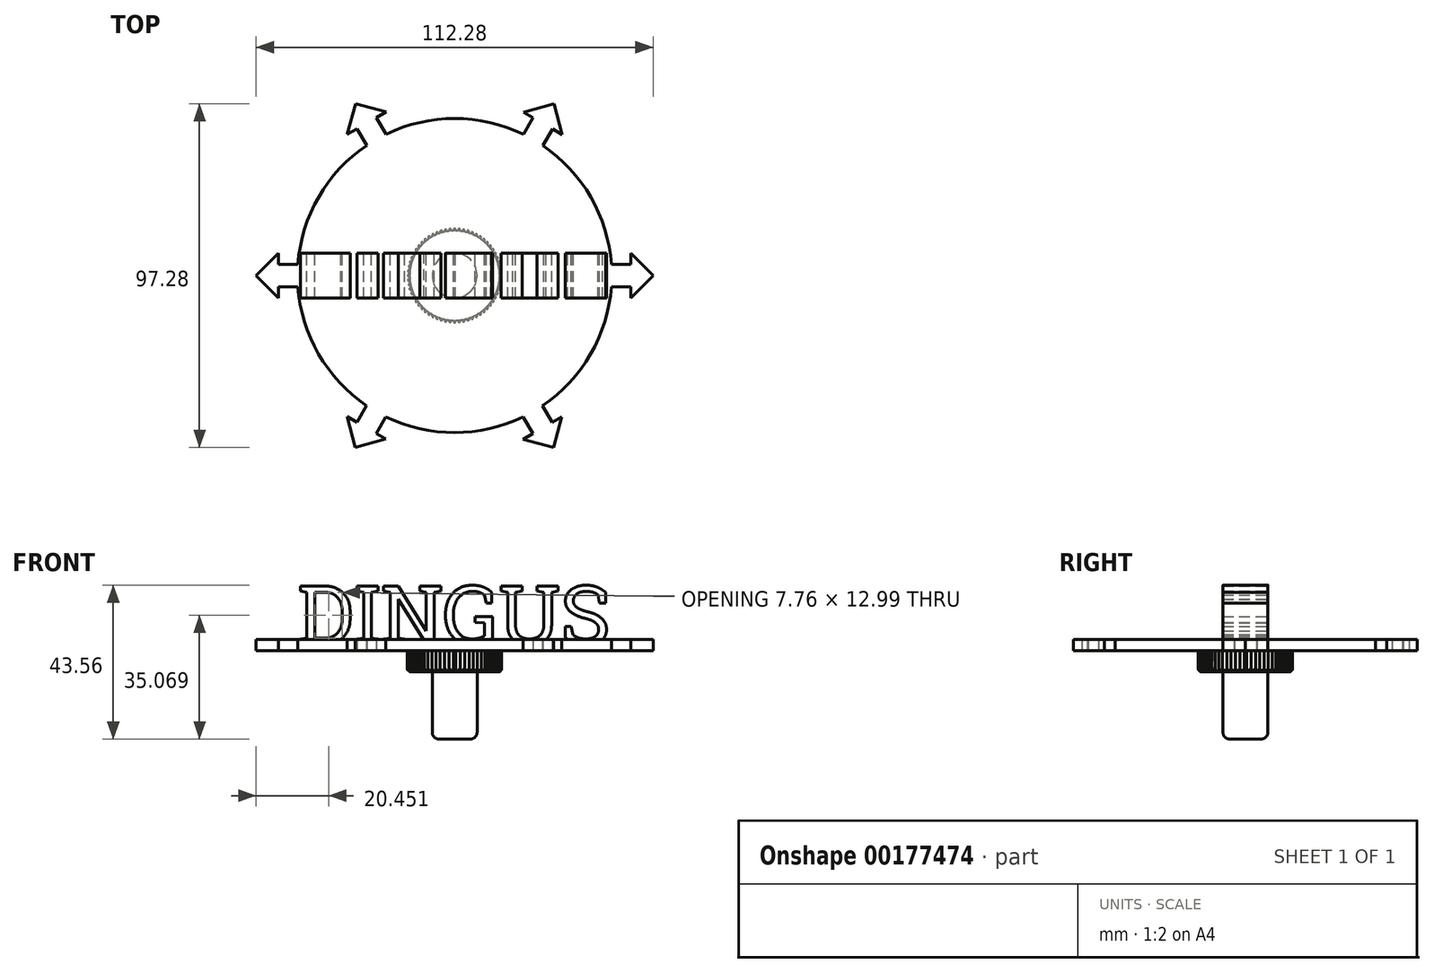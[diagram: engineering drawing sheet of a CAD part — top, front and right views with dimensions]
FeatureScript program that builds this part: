
annotation { "Feature Type Name" : "Feature", "Feature Type Description" : "" }
export const myFeature = defineFeature(function(context is Context, id is Id, definition is map)
    precondition{}
    {
        {
            var Q0;
            Q0=qCreatedBy(makeId("Top.planeOp"),FACE);
            var sketch = newSketch(context, id + "F0", { "sketchPlane" : qUnion([Q0])});
            skCircle(sketch, "E0", {"center": v(0, 0) * mm, "radius": 13.34 * mm, "construction": true});
            skCircle(sketch, "E1", {"center": v(0, 0) * mm, "radius": 12.7 * mm, "construction": true});
            skCircle(sketch, "E2", {"center": v(0, 0) * mm, "radius": 6.35 * mm, "construction": true});
            skLineSegment(sketch, "E3", {"start": v(0, 0) * mm, "end": v(0, 13.34) * mm});
            skLineSegment(sketch, "E4", {"start": v(0, 0) * mm, "end": v(-0.65, 13.32) * mm, "construction": true});
            skLineSegment(sketch, "E5", {"start": v(0, 0) * mm, "end": v(0.65, 13.32) * mm, "construction": true});
            skSolve(sketch);
        }
        {
            var Q0;
            Q0=qCreatedBy(makeId("Top.planeOp"),FACE);
            var sketch = newSketch(context, id + "F1", { "sketchPlane" : qUnion([Q0])});
            skArc(sketch, "E6", {"start": v(0.32, 13.01) * mm, "mid": v(0, 13.34) * mm, "end": v(-0.32, 13.01) * mm});
            skArc(sketch, "E7", {"start": v(-0.62, 12.68) * mm, "mid": v(-0.4, 12.79) * mm, "end": v(-0.32, 13.01) * mm});
            skArc(sketch, "E8", {"start": v(0.32, 13.01) * mm, "mid": v(0.4, 12.79) * mm, "end": v(0.62, 12.68) * mm});
            skArc(sketch, "E9", {"start": v(0.32, 13.01) * mm, "mid": v(0, 13.02) * mm, "end": v(-0.32, 13.01) * mm, "construction": true});
            skArc(sketch, "E10.1.0", {"start": v(-1.86, 12.56) * mm, "mid": v(-1.65, 12.69) * mm, "end": v(-1.59, 12.92) * mm});
            skArc(sketch, "E10.1.1", {"start": v(-0.96, 12.98) * mm, "mid": v(-1.3, 13.27) * mm, "end": v(-1.59, 12.92) * mm});
            skArc(sketch, "E10.1.2", {"start": v(-0.96, 12.98) * mm, "mid": v(-0.85, 12.76) * mm, "end": v(-0.62, 12.68) * mm});
            skArc(sketch, "E10.2.0", {"start": v(-3.09, 12.32) * mm, "mid": v(-2.89, 12.46) * mm, "end": v(-2.85, 12.7) * mm});
            skArc(sketch, "E10.2.1", {"start": v(-2.23, 12.83) * mm, "mid": v(-2.6, 13.08) * mm, "end": v(-2.85, 12.7) * mm});
            skArc(sketch, "E10.2.2", {"start": v(-2.23, 12.83) * mm, "mid": v(-2.1, 12.62) * mm, "end": v(-1.86, 12.56) * mm});
            skArc(sketch, "E10.3.0", {"start": v(-4.28, 11.96) * mm, "mid": v(-4.1, 12.12) * mm, "end": v(-4.08, 12.36) * mm});
            skArc(sketch, "E10.3.1", {"start": v(-3.48, 12.54) * mm, "mid": v(-3.87, 12.76) * mm, "end": v(-4.08, 12.36) * mm});
            skArc(sketch, "E10.3.2", {"start": v(-3.48, 12.54) * mm, "mid": v(-3.33, 12.35) * mm, "end": v(-3.09, 12.32) * mm});
            skArc(sketch, "E10.4.0", {"start": v(-5.43, 11.48) * mm, "mid": v(-5.27, 11.66) * mm, "end": v(-5.27, 11.9) * mm});
            skArc(sketch, "E10.4.1", {"start": v(-4.69, 12.14) * mm, "mid": v(-5.1, 12.32) * mm, "end": v(-5.27, 11.9) * mm});
            skArc(sketch, "E10.4.2", {"start": v(-4.69, 12.14) * mm, "mid": v(-4.52, 11.97) * mm, "end": v(-4.28, 11.96) * mm});
            skArc(sketch, "E10.5.0", {"start": v(-6.53, 10.9) * mm, "mid": v(-6.38, 11.09) * mm, "end": v(-6.41, 11.33) * mm});
            skArc(sketch, "E10.5.1", {"start": v(-5.86, 11.63) * mm, "mid": v(-6.29, 11.76) * mm, "end": v(-6.41, 11.33) * mm});
            skArc(sketch, "E10.5.2", {"start": v(-5.86, 11.63) * mm, "mid": v(-5.67, 11.47) * mm, "end": v(-5.43, 11.48) * mm});
            skArc(sketch, "E10.6.0", {"start": v(-7.57, 10.2) * mm, "mid": v(-7.44, 10.4) * mm, "end": v(-7.5, 10.65) * mm});
            skArc(sketch, "E10.6.1", {"start": v(-6.97, 11) * mm, "mid": v(-7.4, 11.09) * mm, "end": v(-7.5, 10.65) * mm});
            skArc(sketch, "E10.6.2", {"start": v(-6.97, 11) * mm, "mid": v(-6.77, 10.86) * mm, "end": v(-6.53, 10.9) * mm});
            skArc(sketch, "E10.7.0", {"start": v(-8.53, 9.41) * mm, "mid": v(-8.42, 9.63) * mm, "end": v(-8.5, 9.86) * mm});
            skArc(sketch, "E10.7.1", {"start": v(-8.01, 10.26) * mm, "mid": v(-8.46, 10.3) * mm, "end": v(-8.5, 9.86) * mm});
            skArc(sketch, "E10.7.2", {"start": v(-8.01, 10.26) * mm, "mid": v(-7.8, 10.14) * mm, "end": v(-7.57, 10.2) * mm});
            skArc(sketch, "E10.8.0", {"start": v(-9.41, 8.53) * mm, "mid": v(-9.33, 8.76) * mm, "end": v(-9.43, 8.98) * mm});
            skArc(sketch, "E10.8.1", {"start": v(-8.98, 9.43) * mm, "mid": v(-9.43, 9.43) * mm, "end": v(-9.43, 8.98) * mm});
            skArc(sketch, "E10.8.2", {"start": v(-8.98, 9.43) * mm, "mid": v(-8.76, 9.33) * mm, "end": v(-8.53, 9.41) * mm});
            skArc(sketch, "E10.9.0", {"start": v(-10.2, 7.57) * mm, "mid": v(-10.14, 7.8) * mm, "end": v(-10.26, 8.01) * mm});
            skArc(sketch, "E10.9.1", {"start": v(-9.86, 8.5) * mm, "mid": v(-10.3, 8.46) * mm, "end": v(-10.26, 8.01) * mm});
            skArc(sketch, "E10.9.2", {"start": v(-9.86, 8.5) * mm, "mid": v(-9.63, 8.42) * mm, "end": v(-9.41, 8.53) * mm});
            skArc(sketch, "E10.10.0", {"start": v(-10.9, 6.53) * mm, "mid": v(-10.86, 6.77) * mm, "end": v(-11, 6.97) * mm});
            skArc(sketch, "E10.10.1", {"start": v(-10.65, 7.5) * mm, "mid": v(-11.09, 7.4) * mm, "end": v(-11, 6.97) * mm});
            skArc(sketch, "E10.10.2", {"start": v(-10.65, 7.5) * mm, "mid": v(-10.4, 7.44) * mm, "end": v(-10.2, 7.57) * mm});
            skArc(sketch, "E10.11.0", {"start": v(-11.48, 5.43) * mm, "mid": v(-11.47, 5.67) * mm, "end": v(-11.63, 5.86) * mm});
            skArc(sketch, "E10.11.1", {"start": v(-11.33, 6.41) * mm, "mid": v(-11.76, 6.29) * mm, "end": v(-11.63, 5.86) * mm});
            skArc(sketch, "E10.11.2", {"start": v(-11.33, 6.41) * mm, "mid": v(-11.09, 6.38) * mm, "end": v(-10.9, 6.53) * mm});
            skArc(sketch, "E10.12.0", {"start": v(-11.96, 4.28) * mm, "mid": v(-11.97, 4.52) * mm, "end": v(-12.14, 4.69) * mm});
            skArc(sketch, "E10.12.1", {"start": v(-11.9, 5.27) * mm, "mid": v(-12.32, 5.1) * mm, "end": v(-12.14, 4.69) * mm});
            skArc(sketch, "E10.12.2", {"start": v(-11.9, 5.27) * mm, "mid": v(-11.66, 5.27) * mm, "end": v(-11.48, 5.43) * mm});
            skArc(sketch, "E10.13.0", {"start": v(-12.32, 3.09) * mm, "mid": v(-12.35, 3.33) * mm, "end": v(-12.54, 3.48) * mm});
            skArc(sketch, "E10.13.1", {"start": v(-12.36, 4.08) * mm, "mid": v(-12.76, 3.87) * mm, "end": v(-12.54, 3.48) * mm});
            skArc(sketch, "E10.13.2", {"start": v(-12.36, 4.08) * mm, "mid": v(-12.12, 4.1) * mm, "end": v(-11.96, 4.28) * mm});
            skArc(sketch, "E10.14.0", {"start": v(-12.56, 1.86) * mm, "mid": v(-12.62, 2.1) * mm, "end": v(-12.83, 2.23) * mm});
            skArc(sketch, "E10.14.1", {"start": v(-12.7, 2.85) * mm, "mid": v(-13.08, 2.6) * mm, "end": v(-12.83, 2.23) * mm});
            skArc(sketch, "E10.14.2", {"start": v(-12.7, 2.85) * mm, "mid": v(-12.46, 2.89) * mm, "end": v(-12.32, 3.09) * mm});
            skArc(sketch, "E10.15.0", {"start": v(-12.68, 0.62) * mm, "mid": v(-12.76, 0.85) * mm, "end": v(-12.98, 0.96) * mm});
            skArc(sketch, "E10.15.1", {"start": v(-12.92, 1.59) * mm, "mid": v(-13.27, 1.3) * mm, "end": v(-12.98, 0.96) * mm});
            skArc(sketch, "E10.15.2", {"start": v(-12.92, 1.59) * mm, "mid": v(-12.69, 1.65) * mm, "end": v(-12.56, 1.86) * mm});
            skArc(sketch, "E10.16.0", {"start": v(-12.68, -0.62) * mm, "mid": v(-12.79, -0.4) * mm, "end": v(-13.01, -0.32) * mm});
            skArc(sketch, "E10.16.1", {"start": v(-13.01, 0.32) * mm, "mid": v(-13.34, 0) * mm, "end": v(-13.01, -0.32) * mm});
            skArc(sketch, "E10.16.2", {"start": v(-13.01, 0.32) * mm, "mid": v(-12.79, 0.4) * mm, "end": v(-12.68, 0.62) * mm});
            skArc(sketch, "E10.17.0", {"start": v(-12.56, -1.86) * mm, "mid": v(-12.69, -1.65) * mm, "end": v(-12.92, -1.59) * mm});
            skArc(sketch, "E10.17.1", {"start": v(-12.98, -0.96) * mm, "mid": v(-13.27, -1.3) * mm, "end": v(-12.92, -1.59) * mm});
            skArc(sketch, "E10.17.2", {"start": v(-12.98, -0.96) * mm, "mid": v(-12.76, -0.85) * mm, "end": v(-12.68, -0.62) * mm});
            skArc(sketch, "E10.18.0", {"start": v(-12.32, -3.09) * mm, "mid": v(-12.46, -2.89) * mm, "end": v(-12.7, -2.85) * mm});
            skArc(sketch, "E10.18.1", {"start": v(-12.83, -2.23) * mm, "mid": v(-13.08, -2.6) * mm, "end": v(-12.7, -2.85) * mm});
            skArc(sketch, "E10.18.2", {"start": v(-12.83, -2.23) * mm, "mid": v(-12.62, -2.1) * mm, "end": v(-12.56, -1.86) * mm});
            skArc(sketch, "E10.19.0", {"start": v(-11.96, -4.28) * mm, "mid": v(-12.12, -4.1) * mm, "end": v(-12.36, -4.08) * mm});
            skArc(sketch, "E10.19.1", {"start": v(-12.54, -3.48) * mm, "mid": v(-12.76, -3.87) * mm, "end": v(-12.36, -4.08) * mm});
            skArc(sketch, "E10.19.2", {"start": v(-12.54, -3.48) * mm, "mid": v(-12.35, -3.33) * mm, "end": v(-12.32, -3.09) * mm});
            skArc(sketch, "E10.20.0", {"start": v(-11.48, -5.43) * mm, "mid": v(-11.66, -5.27) * mm, "end": v(-11.9, -5.27) * mm});
            skArc(sketch, "E10.20.1", {"start": v(-12.14, -4.69) * mm, "mid": v(-12.32, -5.1) * mm, "end": v(-11.9, -5.27) * mm});
            skArc(sketch, "E10.20.2", {"start": v(-12.14, -4.69) * mm, "mid": v(-11.97, -4.52) * mm, "end": v(-11.96, -4.28) * mm});
            skArc(sketch, "E10.21.0", {"start": v(-10.9, -6.53) * mm, "mid": v(-11.09, -6.38) * mm, "end": v(-11.33, -6.41) * mm});
            skArc(sketch, "E10.21.1", {"start": v(-11.63, -5.86) * mm, "mid": v(-11.76, -6.29) * mm, "end": v(-11.33, -6.41) * mm});
            skArc(sketch, "E10.21.2", {"start": v(-11.63, -5.86) * mm, "mid": v(-11.47, -5.67) * mm, "end": v(-11.48, -5.43) * mm});
            skArc(sketch, "E10.22.0", {"start": v(-10.2, -7.57) * mm, "mid": v(-10.4, -7.44) * mm, "end": v(-10.65, -7.5) * mm});
            skArc(sketch, "E10.22.1", {"start": v(-11, -6.97) * mm, "mid": v(-11.09, -7.4) * mm, "end": v(-10.65, -7.5) * mm});
            skArc(sketch, "E10.22.2", {"start": v(-11, -6.97) * mm, "mid": v(-10.86, -6.77) * mm, "end": v(-10.9, -6.53) * mm});
            skArc(sketch, "E10.23.0", {"start": v(-9.41, -8.53) * mm, "mid": v(-9.63, -8.42) * mm, "end": v(-9.86, -8.5) * mm});
            skArc(sketch, "E10.23.1", {"start": v(-10.26, -8.01) * mm, "mid": v(-10.3, -8.46) * mm, "end": v(-9.86, -8.5) * mm});
            skArc(sketch, "E10.23.2", {"start": v(-10.26, -8.01) * mm, "mid": v(-10.14, -7.8) * mm, "end": v(-10.2, -7.57) * mm});
            skArc(sketch, "E10.24.0", {"start": v(-8.53, -9.41) * mm, "mid": v(-8.76, -9.33) * mm, "end": v(-8.98, -9.43) * mm});
            skArc(sketch, "E10.24.1", {"start": v(-9.43, -8.98) * mm, "mid": v(-9.43, -9.43) * mm, "end": v(-8.98, -9.43) * mm});
            skArc(sketch, "E10.24.2", {"start": v(-9.43, -8.98) * mm, "mid": v(-9.33, -8.76) * mm, "end": v(-9.41, -8.53) * mm});
            skArc(sketch, "E10.25.0", {"start": v(-7.57, -10.2) * mm, "mid": v(-7.8, -10.14) * mm, "end": v(-8.01, -10.26) * mm});
            skArc(sketch, "E10.25.1", {"start": v(-8.5, -9.86) * mm, "mid": v(-8.46, -10.3) * mm, "end": v(-8.01, -10.26) * mm});
            skArc(sketch, "E10.25.2", {"start": v(-8.5, -9.86) * mm, "mid": v(-8.42, -9.63) * mm, "end": v(-8.53, -9.41) * mm});
            skArc(sketch, "E10.26.0", {"start": v(-6.53, -10.9) * mm, "mid": v(-6.77, -10.86) * mm, "end": v(-6.97, -11) * mm});
            skArc(sketch, "E10.26.1", {"start": v(-7.5, -10.65) * mm, "mid": v(-7.4, -11.09) * mm, "end": v(-6.97, -11) * mm});
            skArc(sketch, "E10.26.2", {"start": v(-7.5, -10.65) * mm, "mid": v(-7.44, -10.4) * mm, "end": v(-7.57, -10.2) * mm});
            skArc(sketch, "E10.27.0", {"start": v(-5.43, -11.48) * mm, "mid": v(-5.67, -11.47) * mm, "end": v(-5.86, -11.63) * mm});
            skArc(sketch, "E10.27.1", {"start": v(-6.41, -11.33) * mm, "mid": v(-6.29, -11.76) * mm, "end": v(-5.86, -11.63) * mm});
            skArc(sketch, "E10.27.2", {"start": v(-6.41, -11.33) * mm, "mid": v(-6.38, -11.09) * mm, "end": v(-6.53, -10.9) * mm});
            skArc(sketch, "E10.28.0", {"start": v(-4.28, -11.96) * mm, "mid": v(-4.52, -11.97) * mm, "end": v(-4.69, -12.14) * mm});
            skArc(sketch, "E10.28.1", {"start": v(-5.27, -11.9) * mm, "mid": v(-5.1, -12.32) * mm, "end": v(-4.69, -12.14) * mm});
            skArc(sketch, "E10.28.2", {"start": v(-5.27, -11.9) * mm, "mid": v(-5.27, -11.66) * mm, "end": v(-5.43, -11.48) * mm});
            skArc(sketch, "E10.29.0", {"start": v(-3.09, -12.32) * mm, "mid": v(-3.33, -12.35) * mm, "end": v(-3.48, -12.54) * mm});
            skArc(sketch, "E10.29.1", {"start": v(-4.08, -12.36) * mm, "mid": v(-3.87, -12.76) * mm, "end": v(-3.48, -12.54) * mm});
            skArc(sketch, "E10.29.2", {"start": v(-4.08, -12.36) * mm, "mid": v(-4.1, -12.12) * mm, "end": v(-4.28, -11.96) * mm});
            skArc(sketch, "E10.30.0", {"start": v(-1.86, -12.56) * mm, "mid": v(-2.1, -12.62) * mm, "end": v(-2.23, -12.83) * mm});
            skArc(sketch, "E10.30.1", {"start": v(-2.85, -12.7) * mm, "mid": v(-2.6, -13.08) * mm, "end": v(-2.23, -12.83) * mm});
            skArc(sketch, "E10.30.2", {"start": v(-2.85, -12.7) * mm, "mid": v(-2.89, -12.46) * mm, "end": v(-3.09, -12.32) * mm});
            skArc(sketch, "E10.31.0", {"start": v(-0.62, -12.68) * mm, "mid": v(-0.85, -12.76) * mm, "end": v(-0.96, -12.98) * mm});
            skArc(sketch, "E10.31.1", {"start": v(-1.59, -12.92) * mm, "mid": v(-1.3, -13.27) * mm, "end": v(-0.96, -12.98) * mm});
            skArc(sketch, "E10.31.2", {"start": v(-1.59, -12.92) * mm, "mid": v(-1.65, -12.69) * mm, "end": v(-1.86, -12.56) * mm});
            skPoint(sketch, "E10.center", {"position": v(0, 0) * mm});
            skArc(sketch, "E11.2.32.0", {"start": v(0.62, -12.68) * mm, "mid": v(0.4, -12.79) * mm, "end": v(0.32, -13.01) * mm});
            skArc(sketch, "E11.4.32.0", {"start": v(-0.32, -13.01) * mm, "mid": v(0, -13.34) * mm, "end": v(0.32, -13.01) * mm});
            skArc(sketch, "E11.8.32.0", {"start": v(-0.32, -13.01) * mm, "mid": v(-0.4, -12.79) * mm, "end": v(-0.62, -12.68) * mm});
            skArc(sketch, "E11.2.33.0", {"start": v(1.86, -12.56) * mm, "mid": v(1.65, -12.69) * mm, "end": v(1.59, -12.92) * mm});
            skArc(sketch, "E11.4.33.0", {"start": v(0.96, -12.98) * mm, "mid": v(1.3, -13.27) * mm, "end": v(1.59, -12.92) * mm});
            skArc(sketch, "E11.8.33.0", {"start": v(0.96, -12.98) * mm, "mid": v(0.85, -12.76) * mm, "end": v(0.62, -12.68) * mm});
            skArc(sketch, "E11.2.34.0", {"start": v(3.09, -12.32) * mm, "mid": v(2.89, -12.46) * mm, "end": v(2.85, -12.7) * mm});
            skArc(sketch, "E11.4.34.0", {"start": v(2.23, -12.83) * mm, "mid": v(2.6, -13.08) * mm, "end": v(2.85, -12.7) * mm});
            skArc(sketch, "E11.8.34.0", {"start": v(2.23, -12.83) * mm, "mid": v(2.1, -12.62) * mm, "end": v(1.86, -12.56) * mm});
            skArc(sketch, "E11.2.35.0", {"start": v(4.28, -11.96) * mm, "mid": v(4.1, -12.12) * mm, "end": v(4.08, -12.36) * mm});
            skArc(sketch, "E11.4.35.0", {"start": v(3.48, -12.54) * mm, "mid": v(3.87, -12.76) * mm, "end": v(4.08, -12.36) * mm});
            skArc(sketch, "E11.8.35.0", {"start": v(3.48, -12.54) * mm, "mid": v(3.33, -12.35) * mm, "end": v(3.09, -12.32) * mm});
            skArc(sketch, "E11.2.36.0", {"start": v(5.43, -11.48) * mm, "mid": v(5.27, -11.66) * mm, "end": v(5.27, -11.9) * mm});
            skArc(sketch, "E11.4.36.0", {"start": v(4.69, -12.14) * mm, "mid": v(5.1, -12.32) * mm, "end": v(5.27, -11.9) * mm});
            skArc(sketch, "E11.8.36.0", {"start": v(4.69, -12.14) * mm, "mid": v(4.52, -11.97) * mm, "end": v(4.28, -11.96) * mm});
            skArc(sketch, "E11.2.37.0", {"start": v(6.53, -10.9) * mm, "mid": v(6.38, -11.09) * mm, "end": v(6.41, -11.33) * mm});
            skArc(sketch, "E11.4.37.0", {"start": v(5.86, -11.63) * mm, "mid": v(6.29, -11.76) * mm, "end": v(6.41, -11.33) * mm});
            skArc(sketch, "E11.8.37.0", {"start": v(5.86, -11.63) * mm, "mid": v(5.67, -11.47) * mm, "end": v(5.43, -11.48) * mm});
            skArc(sketch, "E11.2.38.0", {"start": v(7.57, -10.2) * mm, "mid": v(7.44, -10.4) * mm, "end": v(7.5, -10.65) * mm});
            skArc(sketch, "E11.4.38.0", {"start": v(6.97, -11) * mm, "mid": v(7.4, -11.09) * mm, "end": v(7.5, -10.65) * mm});
            skArc(sketch, "E11.8.38.0", {"start": v(6.97, -11) * mm, "mid": v(6.77, -10.86) * mm, "end": v(6.53, -10.9) * mm});
            skArc(sketch, "E11.2.39.0", {"start": v(8.53, -9.41) * mm, "mid": v(8.42, -9.63) * mm, "end": v(8.5, -9.86) * mm});
            skArc(sketch, "E11.4.39.0", {"start": v(8.01, -10.26) * mm, "mid": v(8.46, -10.3) * mm, "end": v(8.5, -9.86) * mm});
            skArc(sketch, "E11.8.39.0", {"start": v(8.01, -10.26) * mm, "mid": v(7.8, -10.14) * mm, "end": v(7.57, -10.2) * mm});
            skArc(sketch, "E11.2.40.0", {"start": v(9.41, -8.53) * mm, "mid": v(9.33, -8.76) * mm, "end": v(9.43, -8.98) * mm});
            skArc(sketch, "E11.4.40.0", {"start": v(8.98, -9.43) * mm, "mid": v(9.43, -9.43) * mm, "end": v(9.43, -8.98) * mm});
            skArc(sketch, "E11.8.40.0", {"start": v(8.98, -9.43) * mm, "mid": v(8.76, -9.33) * mm, "end": v(8.53, -9.41) * mm});
            skArc(sketch, "E11.2.41.0", {"start": v(10.2, -7.57) * mm, "mid": v(10.14, -7.8) * mm, "end": v(10.26, -8.01) * mm});
            skArc(sketch, "E11.4.41.0", {"start": v(9.86, -8.5) * mm, "mid": v(10.3, -8.46) * mm, "end": v(10.26, -8.01) * mm});
            skArc(sketch, "E11.8.41.0", {"start": v(9.86, -8.5) * mm, "mid": v(9.63, -8.42) * mm, "end": v(9.41, -8.53) * mm});
            skArc(sketch, "E11.2.42.0", {"start": v(10.9, -6.53) * mm, "mid": v(10.86, -6.77) * mm, "end": v(11, -6.97) * mm});
            skArc(sketch, "E11.4.42.0", {"start": v(10.65, -7.5) * mm, "mid": v(11.09, -7.4) * mm, "end": v(11, -6.97) * mm});
            skArc(sketch, "E11.8.42.0", {"start": v(10.65, -7.5) * mm, "mid": v(10.4, -7.44) * mm, "end": v(10.2, -7.57) * mm});
            skArc(sketch, "E11.2.43.0", {"start": v(11.48, -5.43) * mm, "mid": v(11.47, -5.67) * mm, "end": v(11.63, -5.86) * mm});
            skArc(sketch, "E11.4.43.0", {"start": v(11.33, -6.41) * mm, "mid": v(11.76, -6.29) * mm, "end": v(11.63, -5.86) * mm});
            skArc(sketch, "E11.8.43.0", {"start": v(11.33, -6.41) * mm, "mid": v(11.09, -6.38) * mm, "end": v(10.9, -6.53) * mm});
            skArc(sketch, "E11.2.44.0", {"start": v(11.96, -4.28) * mm, "mid": v(11.97, -4.52) * mm, "end": v(12.14, -4.69) * mm});
            skArc(sketch, "E11.4.44.0", {"start": v(11.9, -5.27) * mm, "mid": v(12.32, -5.1) * mm, "end": v(12.14, -4.69) * mm});
            skArc(sketch, "E11.8.44.0", {"start": v(11.9, -5.27) * mm, "mid": v(11.66, -5.27) * mm, "end": v(11.48, -5.43) * mm});
            skArc(sketch, "E11.2.45.0", {"start": v(12.32, -3.09) * mm, "mid": v(12.35, -3.33) * mm, "end": v(12.54, -3.48) * mm});
            skArc(sketch, "E11.4.45.0", {"start": v(12.36, -4.08) * mm, "mid": v(12.76, -3.87) * mm, "end": v(12.54, -3.48) * mm});
            skArc(sketch, "E11.8.45.0", {"start": v(12.36, -4.08) * mm, "mid": v(12.12, -4.1) * mm, "end": v(11.96, -4.28) * mm});
            skArc(sketch, "E11.2.46.0", {"start": v(12.56, -1.86) * mm, "mid": v(12.62, -2.1) * mm, "end": v(12.83, -2.23) * mm});
            skArc(sketch, "E11.4.46.0", {"start": v(12.7, -2.85) * mm, "mid": v(13.08, -2.6) * mm, "end": v(12.83, -2.23) * mm});
            skArc(sketch, "E11.8.46.0", {"start": v(12.7, -2.85) * mm, "mid": v(12.46, -2.89) * mm, "end": v(12.32, -3.09) * mm});
            skArc(sketch, "E11.2.47.0", {"start": v(12.68, -0.62) * mm, "mid": v(12.76, -0.85) * mm, "end": v(12.98, -0.96) * mm});
            skArc(sketch, "E11.4.47.0", {"start": v(12.92, -1.59) * mm, "mid": v(13.27, -1.3) * mm, "end": v(12.98, -0.96) * mm});
            skArc(sketch, "E11.8.47.0", {"start": v(12.92, -1.59) * mm, "mid": v(12.69, -1.65) * mm, "end": v(12.56, -1.86) * mm});
            skArc(sketch, "E11.2.48.0", {"start": v(12.68, 0.62) * mm, "mid": v(12.79, 0.4) * mm, "end": v(13.01, 0.32) * mm});
            skArc(sketch, "E11.4.48.0", {"start": v(13.01, -0.32) * mm, "mid": v(13.34, 0) * mm, "end": v(13.01, 0.32) * mm});
            skArc(sketch, "E11.8.48.0", {"start": v(13.01, -0.32) * mm, "mid": v(12.79, -0.4) * mm, "end": v(12.68, -0.62) * mm});
            skArc(sketch, "E11.2.49.0", {"start": v(12.56, 1.86) * mm, "mid": v(12.69, 1.65) * mm, "end": v(12.92, 1.59) * mm});
            skArc(sketch, "E11.4.49.0", {"start": v(12.98, 0.96) * mm, "mid": v(13.27, 1.3) * mm, "end": v(12.92, 1.59) * mm});
            skArc(sketch, "E11.8.49.0", {"start": v(12.98, 0.96) * mm, "mid": v(12.76, 0.85) * mm, "end": v(12.68, 0.62) * mm});
            skArc(sketch, "E11.2.50.0", {"start": v(12.32, 3.09) * mm, "mid": v(12.46, 2.89) * mm, "end": v(12.7, 2.85) * mm});
            skArc(sketch, "E11.4.50.0", {"start": v(12.83, 2.23) * mm, "mid": v(13.08, 2.6) * mm, "end": v(12.7, 2.85) * mm});
            skArc(sketch, "E11.8.50.0", {"start": v(12.83, 2.23) * mm, "mid": v(12.62, 2.1) * mm, "end": v(12.56, 1.86) * mm});
            skArc(sketch, "E11.2.51.0", {"start": v(11.96, 4.28) * mm, "mid": v(12.12, 4.1) * mm, "end": v(12.36, 4.08) * mm});
            skArc(sketch, "E11.4.51.0", {"start": v(12.54, 3.48) * mm, "mid": v(12.76, 3.87) * mm, "end": v(12.36, 4.08) * mm});
            skArc(sketch, "E11.8.51.0", {"start": v(12.54, 3.48) * mm, "mid": v(12.35, 3.33) * mm, "end": v(12.32, 3.09) * mm});
            skArc(sketch, "E11.2.52.0", {"start": v(11.48, 5.43) * mm, "mid": v(11.66, 5.27) * mm, "end": v(11.9, 5.27) * mm});
            skArc(sketch, "E11.4.52.0", {"start": v(12.14, 4.69) * mm, "mid": v(12.32, 5.1) * mm, "end": v(11.9, 5.27) * mm});
            skArc(sketch, "E11.8.52.0", {"start": v(12.14, 4.69) * mm, "mid": v(11.97, 4.52) * mm, "end": v(11.96, 4.28) * mm});
            skArc(sketch, "E11.2.53.0", {"start": v(10.9, 6.53) * mm, "mid": v(11.09, 6.38) * mm, "end": v(11.33, 6.41) * mm});
            skArc(sketch, "E11.4.53.0", {"start": v(11.63, 5.86) * mm, "mid": v(11.76, 6.29) * mm, "end": v(11.33, 6.41) * mm});
            skArc(sketch, "E11.8.53.0", {"start": v(11.63, 5.86) * mm, "mid": v(11.47, 5.67) * mm, "end": v(11.48, 5.43) * mm});
            skArc(sketch, "E11.2.54.0", {"start": v(10.2, 7.57) * mm, "mid": v(10.4, 7.44) * mm, "end": v(10.65, 7.5) * mm});
            skArc(sketch, "E11.4.54.0", {"start": v(11, 6.97) * mm, "mid": v(11.09, 7.4) * mm, "end": v(10.65, 7.5) * mm});
            skArc(sketch, "E11.8.54.0", {"start": v(11, 6.97) * mm, "mid": v(10.86, 6.77) * mm, "end": v(10.9, 6.53) * mm});
            skArc(sketch, "E11.2.55.0", {"start": v(9.41, 8.53) * mm, "mid": v(9.63, 8.42) * mm, "end": v(9.86, 8.5) * mm});
            skArc(sketch, "E11.4.55.0", {"start": v(10.26, 8.01) * mm, "mid": v(10.3, 8.46) * mm, "end": v(9.86, 8.5) * mm});
            skArc(sketch, "E11.8.55.0", {"start": v(10.26, 8.01) * mm, "mid": v(10.14, 7.8) * mm, "end": v(10.2, 7.57) * mm});
            skArc(sketch, "E11.2.56.0", {"start": v(8.53, 9.41) * mm, "mid": v(8.76, 9.33) * mm, "end": v(8.98, 9.43) * mm});
            skArc(sketch, "E11.4.56.0", {"start": v(9.43, 8.98) * mm, "mid": v(9.43, 9.43) * mm, "end": v(8.98, 9.43) * mm});
            skArc(sketch, "E11.8.56.0", {"start": v(9.43, 8.98) * mm, "mid": v(9.33, 8.76) * mm, "end": v(9.41, 8.53) * mm});
            skArc(sketch, "E11.2.57.0", {"start": v(7.57, 10.2) * mm, "mid": v(7.8, 10.14) * mm, "end": v(8.01, 10.26) * mm});
            skArc(sketch, "E11.4.57.0", {"start": v(8.5, 9.86) * mm, "mid": v(8.46, 10.3) * mm, "end": v(8.01, 10.26) * mm});
            skArc(sketch, "E11.8.57.0", {"start": v(8.5, 9.86) * mm, "mid": v(8.42, 9.63) * mm, "end": v(8.53, 9.41) * mm});
            skArc(sketch, "E11.2.58.0", {"start": v(6.53, 10.9) * mm, "mid": v(6.77, 10.86) * mm, "end": v(6.97, 11) * mm});
            skArc(sketch, "E11.4.58.0", {"start": v(7.5, 10.65) * mm, "mid": v(7.4, 11.09) * mm, "end": v(6.97, 11) * mm});
            skArc(sketch, "E11.8.58.0", {"start": v(7.5, 10.65) * mm, "mid": v(7.44, 10.4) * mm, "end": v(7.57, 10.2) * mm});
            skArc(sketch, "E11.2.59.0", {"start": v(5.43, 11.48) * mm, "mid": v(5.67, 11.47) * mm, "end": v(5.86, 11.63) * mm});
            skArc(sketch, "E11.4.59.0", {"start": v(6.41, 11.33) * mm, "mid": v(6.29, 11.76) * mm, "end": v(5.86, 11.63) * mm});
            skArc(sketch, "E11.8.59.0", {"start": v(6.41, 11.33) * mm, "mid": v(6.38, 11.09) * mm, "end": v(6.53, 10.9) * mm});
            skArc(sketch, "E11.2.60.0", {"start": v(4.28, 11.96) * mm, "mid": v(4.52, 11.97) * mm, "end": v(4.69, 12.14) * mm});
            skArc(sketch, "E11.4.60.0", {"start": v(5.27, 11.9) * mm, "mid": v(5.1, 12.32) * mm, "end": v(4.69, 12.14) * mm});
            skArc(sketch, "E11.8.60.0", {"start": v(5.27, 11.9) * mm, "mid": v(5.27, 11.66) * mm, "end": v(5.43, 11.48) * mm});
            skArc(sketch, "E11.2.61.0", {"start": v(3.09, 12.32) * mm, "mid": v(3.33, 12.35) * mm, "end": v(3.48, 12.54) * mm});
            skArc(sketch, "E11.4.61.0", {"start": v(4.08, 12.36) * mm, "mid": v(3.87, 12.76) * mm, "end": v(3.48, 12.54) * mm});
            skArc(sketch, "E11.8.61.0", {"start": v(4.08, 12.36) * mm, "mid": v(4.1, 12.12) * mm, "end": v(4.28, 11.96) * mm});
            skArc(sketch, "E11.2.62.0", {"start": v(1.86, 12.56) * mm, "mid": v(2.1, 12.62) * mm, "end": v(2.23, 12.83) * mm});
            skArc(sketch, "E11.4.62.0", {"start": v(2.85, 12.7) * mm, "mid": v(2.6, 13.08) * mm, "end": v(2.23, 12.83) * mm});
            skArc(sketch, "E11.8.62.0", {"start": v(2.85, 12.7) * mm, "mid": v(2.89, 12.46) * mm, "end": v(3.09, 12.32) * mm});
            skArc(sketch, "E11.2.63.0", {"start": v(0.62, 12.68) * mm, "mid": v(0.85, 12.76) * mm, "end": v(0.96, 12.98) * mm});
            skArc(sketch, "E11.4.63.0", {"start": v(1.59, 12.92) * mm, "mid": v(1.3, 13.27) * mm, "end": v(0.96, 12.98) * mm});
            skArc(sketch, "E11.8.63.0", {"start": v(1.59, 12.92) * mm, "mid": v(1.65, 12.69) * mm, "end": v(1.86, 12.56) * mm});
            skSolve(sketch);
        }
        {
            var Q0;
            Q0=makeQuery(id+"F1.imprint","IMPRINT",FACE,{"disambiguationData":[TD([[makeQuery(id+"F1.imprint","IMPRINT",EDGE,{"derivedFrom":sQuery(id+"F1.wireOp",EDGE,"E6")}),1.0]])]});
            extrude(context, id + "F2", {"entities" : qUnion([Q0]), "depth" : 6 * mm});
        }
        {
            var Q0;
            Q0=makeQuery(id+"F2.opExtrude","CAP_FACE",FACE,{"disambiguationData":[OSD([sQuery(id+"F1.wireOp",EDGE,"E6"),sQuery(id+"F1.wireOp",EDGE,"E7"),sQuery(id+"F1.wireOp",EDGE,"E8"),sQuery(id+"F1.wireOp",EDGE,"E10.1.0"),sQuery(id+"F1.wireOp",EDGE,"E10.1.1"),sQuery(id+"F1.wireOp",EDGE,"E10.1.2"),sQuery(id+"F1.wireOp",EDGE,"E10.2.0"),sQuery(id+"F1.wireOp",EDGE,"E10.2.1"),sQuery(id+"F1.wireOp",EDGE,"E10.2.2"),sQuery(id+"F1.wireOp",EDGE,"E10.3.0"),sQuery(id+"F1.wireOp",EDGE,"E10.3.1"),sQuery(id+"F1.wireOp",EDGE,"E10.3.2"),sQuery(id+"F1.wireOp",EDGE,"E10.4.0"),sQuery(id+"F1.wireOp",EDGE,"E10.4.1"),sQuery(id+"F1.wireOp",EDGE,"E10.4.2"),sQuery(id+"F1.wireOp",EDGE,"E10.5.0"),sQuery(id+"F1.wireOp",EDGE,"E10.5.1"),sQuery(id+"F1.wireOp",EDGE,"E10.5.2"),sQuery(id+"F1.wireOp",EDGE,"E10.6.0"),sQuery(id+"F1.wireOp",EDGE,"E10.6.1"),sQuery(id+"F1.wireOp",EDGE,"E10.6.2"),sQuery(id+"F1.wireOp",EDGE,"E10.7.0"),sQuery(id+"F1.wireOp",EDGE,"E10.7.1"),sQuery(id+"F1.wireOp",EDGE,"E10.7.2"),sQuery(id+"F1.wireOp",EDGE,"E10.8.0"),sQuery(id+"F1.wireOp",EDGE,"E10.8.1"),sQuery(id+"F1.wireOp",EDGE,"E10.8.2"),sQuery(id+"F1.wireOp",EDGE,"E10.9.0"),sQuery(id+"F1.wireOp",EDGE,"E10.9.1"),sQuery(id+"F1.wireOp",EDGE,"E10.9.2"),sQuery(id+"F1.wireOp",EDGE,"E10.10.0"),sQuery(id+"F1.wireOp",EDGE,"E10.10.1"),sQuery(id+"F1.wireOp",EDGE,"E10.10.2"),sQuery(id+"F1.wireOp",EDGE,"E10.11.0"),sQuery(id+"F1.wireOp",EDGE,"E10.11.1"),sQuery(id+"F1.wireOp",EDGE,"E10.11.2"),sQuery(id+"F1.wireOp",EDGE,"E10.12.0"),sQuery(id+"F1.wireOp",EDGE,"E10.12.1"),sQuery(id+"F1.wireOp",EDGE,"E10.12.2"),sQuery(id+"F1.wireOp",EDGE,"E10.13.0"),sQuery(id+"F1.wireOp",EDGE,"E10.13.1"),sQuery(id+"F1.wireOp",EDGE,"E10.13.2"),sQuery(id+"F1.wireOp",EDGE,"E10.14.0"),sQuery(id+"F1.wireOp",EDGE,"E10.14.1"),sQuery(id+"F1.wireOp",EDGE,"E10.14.2"),sQuery(id+"F1.wireOp",EDGE,"E10.15.0"),sQuery(id+"F1.wireOp",EDGE,"E10.15.1"),sQuery(id+"F1.wireOp",EDGE,"E10.15.2"),sQuery(id+"F1.wireOp",EDGE,"E10.16.0"),sQuery(id+"F1.wireOp",EDGE,"E10.16.1"),sQuery(id+"F1.wireOp",EDGE,"E10.16.2"),sQuery(id+"F1.wireOp",EDGE,"E10.17.0"),sQuery(id+"F1.wireOp",EDGE,"E10.17.1"),sQuery(id+"F1.wireOp",EDGE,"E10.17.2"),sQuery(id+"F1.wireOp",EDGE,"E10.18.0"),sQuery(id+"F1.wireOp",EDGE,"E10.18.1"),sQuery(id+"F1.wireOp",EDGE,"E10.18.2"),sQuery(id+"F1.wireOp",EDGE,"E10.19.0"),sQuery(id+"F1.wireOp",EDGE,"E10.19.1"),sQuery(id+"F1.wireOp",EDGE,"E10.19.2"),sQuery(id+"F1.wireOp",EDGE,"E10.20.0"),sQuery(id+"F1.wireOp",EDGE,"E10.20.1"),sQuery(id+"F1.wireOp",EDGE,"E10.20.2"),sQuery(id+"F1.wireOp",EDGE,"E10.21.0"),sQuery(id+"F1.wireOp",EDGE,"E10.21.1"),sQuery(id+"F1.wireOp",EDGE,"E10.21.2"),sQuery(id+"F1.wireOp",EDGE,"E10.22.0"),sQuery(id+"F1.wireOp",EDGE,"E10.22.1"),sQuery(id+"F1.wireOp",EDGE,"E10.22.2"),sQuery(id+"F1.wireOp",EDGE,"E10.23.0"),sQuery(id+"F1.wireOp",EDGE,"E10.23.1"),sQuery(id+"F1.wireOp",EDGE,"E10.23.2"),sQuery(id+"F1.wireOp",EDGE,"E10.24.0"),sQuery(id+"F1.wireOp",EDGE,"E10.24.1"),sQuery(id+"F1.wireOp",EDGE,"E10.24.2"),sQuery(id+"F1.wireOp",EDGE,"E10.25.0"),sQuery(id+"F1.wireOp",EDGE,"E10.25.1"),sQuery(id+"F1.wireOp",EDGE,"E10.25.2"),sQuery(id+"F1.wireOp",EDGE,"E10.26.0"),sQuery(id+"F1.wireOp",EDGE,"E10.26.1"),sQuery(id+"F1.wireOp",EDGE,"E10.26.2"),sQuery(id+"F1.wireOp",EDGE,"E10.27.0"),sQuery(id+"F1.wireOp",EDGE,"E10.27.1"),sQuery(id+"F1.wireOp",EDGE,"E10.27.2"),sQuery(id+"F1.wireOp",EDGE,"E10.28.0"),sQuery(id+"F1.wireOp",EDGE,"E10.28.1"),sQuery(id+"F1.wireOp",EDGE,"E10.28.2"),sQuery(id+"F1.wireOp",EDGE,"E10.29.0"),sQuery(id+"F1.wireOp",EDGE,"E10.29.1"),sQuery(id+"F1.wireOp",EDGE,"E10.29.2"),sQuery(id+"F1.wireOp",EDGE,"E10.30.0"),sQuery(id+"F1.wireOp",EDGE,"E10.30.1"),sQuery(id+"F1.wireOp",EDGE,"E10.30.2"),sQuery(id+"F1.wireOp",EDGE,"E10.31.0"),sQuery(id+"F1.wireOp",EDGE,"E10.31.1"),sQuery(id+"F1.wireOp",EDGE,"E10.31.2")])],"isStart":false});
            var sketch = newSketch(context, id + "F3", { "sketchPlane" : qUnion([Q0])});
            skCircle(sketch, "E12.0", {"center": v(0, 0) * mm, "radius": 6.35 * mm});
            skSolve(sketch);
        }
        {
            var Q0;
            Q0=makeQuery(id+"F2.opExtrude","CAP_FACE",FACE,{"disambiguationData":[OSD([sQuery(id+"F1.wireOp",EDGE,"E6"),sQuery(id+"F1.wireOp",EDGE,"E7"),sQuery(id+"F1.wireOp",EDGE,"E8"),sQuery(id+"F1.wireOp",EDGE,"E10.1.0"),sQuery(id+"F1.wireOp",EDGE,"E10.1.1"),sQuery(id+"F1.wireOp",EDGE,"E10.1.2"),sQuery(id+"F1.wireOp",EDGE,"E10.2.0"),sQuery(id+"F1.wireOp",EDGE,"E10.2.1"),sQuery(id+"F1.wireOp",EDGE,"E10.2.2"),sQuery(id+"F1.wireOp",EDGE,"E10.3.0"),sQuery(id+"F1.wireOp",EDGE,"E10.3.1"),sQuery(id+"F1.wireOp",EDGE,"E10.3.2"),sQuery(id+"F1.wireOp",EDGE,"E10.4.0"),sQuery(id+"F1.wireOp",EDGE,"E10.4.1"),sQuery(id+"F1.wireOp",EDGE,"E10.4.2"),sQuery(id+"F1.wireOp",EDGE,"E10.5.0"),sQuery(id+"F1.wireOp",EDGE,"E10.5.1"),sQuery(id+"F1.wireOp",EDGE,"E10.5.2"),sQuery(id+"F1.wireOp",EDGE,"E10.6.0"),sQuery(id+"F1.wireOp",EDGE,"E10.6.1"),sQuery(id+"F1.wireOp",EDGE,"E10.6.2"),sQuery(id+"F1.wireOp",EDGE,"E10.7.0"),sQuery(id+"F1.wireOp",EDGE,"E10.7.1"),sQuery(id+"F1.wireOp",EDGE,"E10.7.2"),sQuery(id+"F1.wireOp",EDGE,"E10.8.0"),sQuery(id+"F1.wireOp",EDGE,"E10.8.1"),sQuery(id+"F1.wireOp",EDGE,"E10.8.2"),sQuery(id+"F1.wireOp",EDGE,"E10.9.0"),sQuery(id+"F1.wireOp",EDGE,"E10.9.1"),sQuery(id+"F1.wireOp",EDGE,"E10.9.2"),sQuery(id+"F1.wireOp",EDGE,"E10.10.0"),sQuery(id+"F1.wireOp",EDGE,"E10.10.1"),sQuery(id+"F1.wireOp",EDGE,"E10.10.2"),sQuery(id+"F1.wireOp",EDGE,"E10.11.0"),sQuery(id+"F1.wireOp",EDGE,"E10.11.1"),sQuery(id+"F1.wireOp",EDGE,"E10.11.2"),sQuery(id+"F1.wireOp",EDGE,"E10.12.0"),sQuery(id+"F1.wireOp",EDGE,"E10.12.1"),sQuery(id+"F1.wireOp",EDGE,"E10.12.2"),sQuery(id+"F1.wireOp",EDGE,"E10.13.0"),sQuery(id+"F1.wireOp",EDGE,"E10.13.1"),sQuery(id+"F1.wireOp",EDGE,"E10.13.2"),sQuery(id+"F1.wireOp",EDGE,"E10.14.0"),sQuery(id+"F1.wireOp",EDGE,"E10.14.1"),sQuery(id+"F1.wireOp",EDGE,"E10.14.2"),sQuery(id+"F1.wireOp",EDGE,"E10.15.0"),sQuery(id+"F1.wireOp",EDGE,"E10.15.1"),sQuery(id+"F1.wireOp",EDGE,"E10.15.2"),sQuery(id+"F1.wireOp",EDGE,"E10.16.0"),sQuery(id+"F1.wireOp",EDGE,"E10.16.1"),sQuery(id+"F1.wireOp",EDGE,"E10.16.2"),sQuery(id+"F1.wireOp",EDGE,"E10.17.0"),sQuery(id+"F1.wireOp",EDGE,"E10.17.1"),sQuery(id+"F1.wireOp",EDGE,"E10.17.2"),sQuery(id+"F1.wireOp",EDGE,"E10.18.0"),sQuery(id+"F1.wireOp",EDGE,"E10.18.1"),sQuery(id+"F1.wireOp",EDGE,"E10.18.2"),sQuery(id+"F1.wireOp",EDGE,"E10.19.0"),sQuery(id+"F1.wireOp",EDGE,"E10.19.1"),sQuery(id+"F1.wireOp",EDGE,"E10.19.2"),sQuery(id+"F1.wireOp",EDGE,"E10.20.0"),sQuery(id+"F1.wireOp",EDGE,"E10.20.1"),sQuery(id+"F1.wireOp",EDGE,"E10.20.2"),sQuery(id+"F1.wireOp",EDGE,"E10.21.0"),sQuery(id+"F1.wireOp",EDGE,"E10.21.1"),sQuery(id+"F1.wireOp",EDGE,"E10.21.2"),sQuery(id+"F1.wireOp",EDGE,"E10.22.0"),sQuery(id+"F1.wireOp",EDGE,"E10.22.1"),sQuery(id+"F1.wireOp",EDGE,"E10.22.2"),sQuery(id+"F1.wireOp",EDGE,"E10.23.0"),sQuery(id+"F1.wireOp",EDGE,"E10.23.1"),sQuery(id+"F1.wireOp",EDGE,"E10.23.2"),sQuery(id+"F1.wireOp",EDGE,"E10.24.0"),sQuery(id+"F1.wireOp",EDGE,"E10.24.1"),sQuery(id+"F1.wireOp",EDGE,"E10.24.2"),sQuery(id+"F1.wireOp",EDGE,"E10.25.0"),sQuery(id+"F1.wireOp",EDGE,"E10.25.1"),sQuery(id+"F1.wireOp",EDGE,"E10.25.2"),sQuery(id+"F1.wireOp",EDGE,"E10.26.0"),sQuery(id+"F1.wireOp",EDGE,"E10.26.1"),sQuery(id+"F1.wireOp",EDGE,"E10.26.2"),sQuery(id+"F1.wireOp",EDGE,"E10.27.0"),sQuery(id+"F1.wireOp",EDGE,"E10.27.1"),sQuery(id+"F1.wireOp",EDGE,"E10.27.2"),sQuery(id+"F1.wireOp",EDGE,"E10.28.0"),sQuery(id+"F1.wireOp",EDGE,"E10.28.1"),sQuery(id+"F1.wireOp",EDGE,"E10.28.2"),sQuery(id+"F1.wireOp",EDGE,"E10.29.0"),sQuery(id+"F1.wireOp",EDGE,"E10.29.1"),sQuery(id+"F1.wireOp",EDGE,"E10.29.2"),sQuery(id+"F1.wireOp",EDGE,"E10.30.0"),sQuery(id+"F1.wireOp",EDGE,"E10.30.1"),sQuery(id+"F1.wireOp",EDGE,"E10.30.2"),sQuery(id+"F1.wireOp",EDGE,"E10.31.0"),sQuery(id+"F1.wireOp",EDGE,"E10.31.1"),sQuery(id+"F1.wireOp",EDGE,"E10.31.2")])],"isStart":true});
            var sketch = newSketch(context, id + "F4", { "sketchPlane" : qUnion([Q0])});
            skCircle(sketch, "E13", {"center": v(0, 0) * mm, "radius": 47.63 * mm});
            skSolve(sketch);
        }
        {
            var Q0;
            Q0=makeQuery(id+"F4.imprint","IMPRINT",FACE,{"disambiguationData":[TD([[makeQuery(id+"F4.imprint","IMPRINT",EDGE,{"derivedFrom":sQuery(id+"F4.wireOp",EDGE,"E13")}),1.0]])]});
            var sketch = newSketch(context, id + "F5", { "sketchPlane" : qUnion([Q0])});
            skCircle(sketch, "E14.0", {"center": v(0, 0) * mm, "radius": 6.35 * mm});
            skSolve(sketch);
        }
        {
            var Q0;
            Q0 = qSketchRegion(id + "F5", true);
            extrude(context, id + "F6", {"entities" : qUnion([Q0]), "operationType" : NewBodyOperationType.ADD, "depth" : 19.05 * mm});
        }
        {
            var Q0;
            Q0=makeQuery(id+"F3.imprint","IMPRINT",FACE,{"disambiguationData":[TD([[makeQuery(id+"F3.imprint","IMPRINT",EDGE,{"derivedFrom":sQuery(id+"F3.wireOp",EDGE,"E12.0")}),-1.0]])]});
            var sketch = newSketch(context, id + "F7", { "sketchPlane" : qUnion([Q0])});
            skCircle(sketch, "E15", {"center": v(0, 0) * mm, "radius": 44.45 * mm});
            skSolve(sketch);
        }
        {
            var Q0;
            Q0 = qSketchRegion(id + "F7", true);
            extrude(context, id + "F8", {"entities" : qUnion([Q0]), "operationType" : NewBodyOperationType.ADD, "depth" : 3.17 * mm});
        }
        {
            var Q0;
            Q0=qCreatedBy(makeId("Front.planeOp"),FACE);
            var sketch = newSketch(context, id + "F9", { "sketchPlane" : qUnion([Q0])});
            skLineSegment(sketch, "E16.0", {"start": v(-44.45, 9.18) * mm, "end": v(44.45, 9.18) * mm, "construction": true});
            skText(sketch, "E17", { "text": "DINGUS", "fontName": "RobotoSlab-Regular.ttf"});
            const initialGuessF9  = {"E17": [-0.04445, 0.00778, 1, 0, 0.0167]};
            skSetInitialGuess(sketch, initialGuessF9);
            skSolve(sketch);
        }
        {
            var Q0;
            Q0 = qSketchRegion(id + "F9", true);
            extrude(context, id + "F10", {"entities" : qUnion([Q0]), "operationType" : NewBodyOperationType.ADD, "endBound" : BoundingType.SYMMETRIC, "depth" : 12.7 * mm});
        }
        {
            var Q0;
            Q0=makeQuery(id+"F4.imprint","IMPRINT",FACE,{"disambiguationData":[TD([[makeQuery(id+"F4.imprint","IMPRINT",EDGE,{"derivedFrom":sQuery(id+"F4.wireOp",EDGE,"E13")}),1.0]])]});
            var sketch = newSketch(context, id + "F11", { "sketchPlane" : qUnion([Q0])});
            skLineSegment(sketch, "E18", {"start": v(0, 0) * mm, "end": v(-44.1, 0) * mm, "construction": true});
            skLineSegment(sketch, "E19", {"start": v(-44.34, -3.18) * mm, "end": v(-50.69, -3.18) * mm});
            skLineSegment(sketch, "E20", {"start": v(-50.69, -3.18) * mm, "end": v(-50.69, -6.35) * mm});
            skLineSegment(sketch, "E21", {"start": v(-50.69, -6.35) * mm, "end": v(-57.04, 0) * mm});
            skLineSegment(sketch, "E22.MirrorCS", {"start": v(-50.69, 3.18) * mm, "end": v(-50.69, 6.35) * mm});
            skLineSegment(sketch, "E23.MirrorCS", {"start": v(-50.69, 6.35) * mm, "end": v(-57.04, 0) * mm});
            skLineSegment(sketch, "E24.MirrorCS", {"start": v(-44.34, 3.18) * mm, "end": v(-50.69, 3.18) * mm});
            skArc(sketch, "E25.0", {"start": v(-44.34, 3.17) * mm, "mid": v(-44.45, 0) * mm, "end": v(-44.34, -3.17) * mm});
            skLineSegment(sketch, "E26.1.0", {"start": v(-22.6, -45.48) * mm, "end": v(-19.84, -47.07) * mm});
            skLineSegment(sketch, "E26.1.1", {"start": v(-19.84, -47.07) * mm, "end": v(-28.52, -49.4) * mm});
            skLineSegment(sketch, "E26.1.2", {"start": v(-28.1, -42.3) * mm, "end": v(-30.84, -40.72) * mm});
            skLineSegment(sketch, "E26.1.3", {"start": v(-30.84, -40.72) * mm, "end": v(-28.52, -49.4) * mm});
            skLineSegment(sketch, "E26.1.4", {"start": v(-19.42, -39.98) * mm, "end": v(-22.6, -45.48) * mm});
            skLineSegment(sketch, "E26.1.5", {"start": v(-24.92, -36.8) * mm, "end": v(-28.1, -42.3) * mm});
            skArc(sketch, "E26.1.6", {"start": v(-24.92, -36.8) * mm, "mid": v(-22.23, -38.5) * mm, "end": v(-19.42, -39.98) * mm});
            skLineSegment(sketch, "E26.2.0", {"start": v(28.1, -42.3) * mm, "end": v(30.84, -40.72) * mm});
            skLineSegment(sketch, "E26.2.1", {"start": v(30.84, -40.72) * mm, "end": v(28.52, -49.4) * mm});
            skLineSegment(sketch, "E26.2.2", {"start": v(22.6, -45.48) * mm, "end": v(19.84, -47.07) * mm});
            skLineSegment(sketch, "E26.2.3", {"start": v(19.84, -47.07) * mm, "end": v(28.52, -49.4) * mm});
            skLineSegment(sketch, "E26.2.4", {"start": v(24.92, -36.8) * mm, "end": v(28.1, -42.3) * mm});
            skLineSegment(sketch, "E26.2.5", {"start": v(19.42, -39.98) * mm, "end": v(22.6, -45.48) * mm});
            skArc(sketch, "E26.2.6", {"start": v(19.42, -39.98) * mm, "mid": v(22.22, -38.5) * mm, "end": v(24.92, -36.8) * mm});
            skLineSegment(sketch, "E26.3.0", {"start": v(50.69, 3.17) * mm, "end": v(50.69, 6.35) * mm});
            skLineSegment(sketch, "E26.3.1", {"start": v(50.69, 6.35) * mm, "end": v(57.04, 0) * mm});
            skLineSegment(sketch, "E26.3.2", {"start": v(50.69, -3.18) * mm, "end": v(50.69, -6.35) * mm});
            skLineSegment(sketch, "E26.3.3", {"start": v(50.69, -6.35) * mm, "end": v(57.04, 0) * mm});
            skLineSegment(sketch, "E26.3.4", {"start": v(44.34, 3.17) * mm, "end": v(50.69, 3.17) * mm});
            skLineSegment(sketch, "E26.3.5", {"start": v(44.34, -3.18) * mm, "end": v(50.69, -3.18) * mm});
            skArc(sketch, "E26.3.6", {"start": v(44.34, -3.17) * mm, "mid": v(44.45, 0) * mm, "end": v(44.34, 3.17) * mm});
            skLineSegment(sketch, "E26.4.0", {"start": v(22.6, 45.48) * mm, "end": v(19.84, 47.07) * mm});
            skLineSegment(sketch, "E26.4.1", {"start": v(19.84, 47.07) * mm, "end": v(28.52, 49.4) * mm});
            skLineSegment(sketch, "E26.4.2", {"start": v(28.1, 42.3) * mm, "end": v(30.84, 40.72) * mm});
            skLineSegment(sketch, "E26.4.3", {"start": v(30.84, 40.72) * mm, "end": v(28.52, 49.4) * mm});
            skLineSegment(sketch, "E26.4.4", {"start": v(19.42, 39.98) * mm, "end": v(22.6, 45.48) * mm});
            skLineSegment(sketch, "E26.4.5", {"start": v(24.92, 36.8) * mm, "end": v(28.1, 42.3) * mm});
            skArc(sketch, "E26.4.6", {"start": v(24.92, 36.8) * mm, "mid": v(22.23, 38.5) * mm, "end": v(19.42, 39.98) * mm});
            skLineSegment(sketch, "E26.5.0", {"start": v(-28.1, 42.3) * mm, "end": v(-30.84, 40.72) * mm});
            skLineSegment(sketch, "E26.5.1", {"start": v(-30.84, 40.72) * mm, "end": v(-28.52, 49.4) * mm});
            skLineSegment(sketch, "E26.5.2", {"start": v(-22.6, 45.48) * mm, "end": v(-19.84, 47.07) * mm});
            skLineSegment(sketch, "E26.5.3", {"start": v(-19.84, 47.07) * mm, "end": v(-28.52, 49.4) * mm});
            skLineSegment(sketch, "E26.5.4", {"start": v(-24.92, 36.8) * mm, "end": v(-28.1, 42.3) * mm});
            skLineSegment(sketch, "E26.5.5", {"start": v(-19.42, 39.98) * mm, "end": v(-22.6, 45.48) * mm});
            skArc(sketch, "E26.5.6", {"start": v(-19.42, 39.98) * mm, "mid": v(-22.23, 38.5) * mm, "end": v(-24.92, 36.8) * mm});
            skSolve(sketch);
        }
        {
            var Q0;
            Q0=makeQuery(id+"F8.opExtrude","CAP_FACE",FACE,{"disambiguationData":[OSD([sQuery(id+"F7.wireOp",EDGE,"E15")])],"isStart":true});
            var sketch = newSketch(context, id + "F12", { "sketchPlane" : qUnion([Q0])});
            skLineSegment(sketch, "E27", {"start": v(0.9, -0.05) * mm, "end": v(-43.2, -0.05) * mm, "construction": true});
            skLineSegment(sketch, "E28", {"start": v(-43.44, -3.22) * mm, "end": v(-49.8, -3.22) * mm});
            skLineSegment(sketch, "E29", {"start": v(-49.8, -3.22) * mm, "end": v(-49.8, -6.4) * mm});
            skLineSegment(sketch, "E30", {"start": v(-49.8, -6.4) * mm, "end": v(-56.14, -0.05) * mm});
            skLineSegment(sketch, "E31.MirrorCS", {"start": v(-49.8, 3.13) * mm, "end": v(-49.8, 6.3) * mm});
            skLineSegment(sketch, "E32.MirrorCS", {"start": v(-49.8, 6.3) * mm, "end": v(-56.14, -0.05) * mm});
            skLineSegment(sketch, "E33.MirrorCS", {"start": v(-43.44, 3.13) * mm, "end": v(-49.8, 3.13) * mm});
            skArc(sketch, "E34.0", {"start": v(-43.44, 3.13) * mm, "mid": v(-43.56, -0.05) * mm, "end": v(-43.44, -3.22) * mm});
            skLineSegment(sketch, "E35.1.0", {"start": v(-22.1, -44.73) * mm, "end": v(-19.36, -46.32) * mm});
            skLineSegment(sketch, "E35.1.1", {"start": v(-19.36, -46.32) * mm, "end": v(-28.03, -48.64) * mm});
            skLineSegment(sketch, "E35.1.2", {"start": v(-27.6, -41.56) * mm, "end": v(-30.36, -39.97) * mm});
            skLineSegment(sketch, "E35.1.3", {"start": v(-30.36, -39.97) * mm, "end": v(-28.03, -48.64) * mm});
            skLineSegment(sketch, "E35.1.4", {"start": v(-18.93, -39.23) * mm, "end": v(-22.1, -44.73) * mm});
            skLineSegment(sketch, "E35.1.5", {"start": v(-24.43, -36.06) * mm, "end": v(-27.6, -41.56) * mm});
            skArc(sketch, "E35.1.6", {"start": v(-24.43, -36.06) * mm, "mid": v(-21.74, -37.74) * mm, "end": v(-18.93, -39.23) * mm});
            skLineSegment(sketch, "E35.2.0", {"start": v(27.69, -41.51) * mm, "end": v(30.44, -39.92) * mm});
            skLineSegment(sketch, "E35.2.1", {"start": v(30.44, -39.92) * mm, "end": v(28.11, -48.6) * mm});
            skLineSegment(sketch, "E35.2.2", {"start": v(22.19, -44.69) * mm, "end": v(19.44, -46.27) * mm});
            skLineSegment(sketch, "E35.2.3", {"start": v(19.44, -46.27) * mm, "end": v(28.11, -48.6) * mm});
            skLineSegment(sketch, "E35.2.4", {"start": v(24.51, -36.01) * mm, "end": v(27.69, -41.51) * mm});
            skLineSegment(sketch, "E35.2.5", {"start": v(19.01, -39.19) * mm, "end": v(22.19, -44.69) * mm});
            skArc(sketch, "E35.2.6", {"start": v(19.01, -39.19) * mm, "mid": v(21.82, -37.7) * mm, "end": v(24.51, -36.01) * mm});
            skLineSegment(sketch, "E35.3.0", {"start": v(49.8, 3.22) * mm, "end": v(49.8, 6.4) * mm});
            skLineSegment(sketch, "E35.3.1", {"start": v(49.8, 6.4) * mm, "end": v(56.14, 0.05) * mm});
            skLineSegment(sketch, "E35.3.2", {"start": v(49.8, -3.13) * mm, "end": v(49.8, -6.3) * mm});
            skLineSegment(sketch, "E35.3.3", {"start": v(49.8, -6.3) * mm, "end": v(56.14, 0.05) * mm});
            skLineSegment(sketch, "E35.3.4", {"start": v(43.44, 3.22) * mm, "end": v(49.8, 3.22) * mm});
            skLineSegment(sketch, "E35.3.5", {"start": v(43.44, -3.13) * mm, "end": v(49.8, -3.13) * mm});
            skArc(sketch, "E35.3.6", {"start": v(43.44, -3.13) * mm, "mid": v(43.56, 0.05) * mm, "end": v(43.44, 3.22) * mm});
            skLineSegment(sketch, "E35.4.0", {"start": v(22.1, 44.73) * mm, "end": v(19.36, 46.32) * mm});
            skLineSegment(sketch, "E35.4.1", {"start": v(19.36, 46.32) * mm, "end": v(28.03, 48.64) * mm});
            skLineSegment(sketch, "E35.4.2", {"start": v(27.6, 41.56) * mm, "end": v(30.36, 39.97) * mm});
            skLineSegment(sketch, "E35.4.3", {"start": v(30.36, 39.97) * mm, "end": v(28.03, 48.64) * mm});
            skLineSegment(sketch, "E35.4.4", {"start": v(18.93, 39.23) * mm, "end": v(22.1, 44.73) * mm});
            skLineSegment(sketch, "E35.4.5", {"start": v(24.43, 36.06) * mm, "end": v(27.6, 41.56) * mm});
            skArc(sketch, "E35.4.6", {"start": v(24.43, 36.06) * mm, "mid": v(21.74, 37.74) * mm, "end": v(18.93, 39.23) * mm});
            skLineSegment(sketch, "E35.5.0", {"start": v(-27.69, 41.51) * mm, "end": v(-30.44, 39.92) * mm});
            skLineSegment(sketch, "E35.5.1", {"start": v(-30.44, 39.92) * mm, "end": v(-28.11, 48.6) * mm});
            skLineSegment(sketch, "E35.5.2", {"start": v(-22.19, 44.69) * mm, "end": v(-19.44, 46.27) * mm});
            skLineSegment(sketch, "E35.5.3", {"start": v(-19.44, 46.27) * mm, "end": v(-28.11, 48.6) * mm});
            skLineSegment(sketch, "E35.5.4", {"start": v(-24.51, 36.01) * mm, "end": v(-27.69, 41.51) * mm});
            skLineSegment(sketch, "E35.5.5", {"start": v(-19.01, 39.19) * mm, "end": v(-22.19, 44.69) * mm});
            skArc(sketch, "E35.5.6", {"start": v(-19.01, 39.19) * mm, "mid": v(-21.82, 37.7) * mm, "end": v(-24.51, 36.01) * mm});
            skPoint(sketch, "E35.center", {"position": v(0, 0) * mm});
            skSolve(sketch);
        }
        {
            var Q0;
            Q0 = qSketchRegion(id + "F12", true);
            extrude(context, id + "F13", {"entities" : qUnion([Q0]), "operationType" : NewBodyOperationType.ADD, "oppositeDirection" : true, "depth" : 3.17 * mm});
        }
        {
            var Q0;
            Q0=makeQuery(id+"F6.opExtrude","CAP_EDGE",EDGE,{"disambiguationData":[OSD([sQuery(id+"F5.wireOp",EDGE,"E14.0")])],"isStart":false});
            fillet(context, id + "F14", {"entities" : qUnion([Q0]), "radius" : 1.9 * mm, "tangentPropagation" : true, "allowEdgeOverflow" : false});
        }
        {
            var Q0;
            Q0=qCreatedBy(makeId("Front.planeOp"),FACE);
            var sketch = newSketch(context, id + "F15", { "sketchPlane" : qUnion([Q0])});
            skLineSegment(sketch, "E36", {"start": v(12.7, 0) * mm, "end": v(13.34, 0.63) * mm});
            skLineSegment(sketch, "E37", {"start": v(13.34, 0.64) * mm, "end": v(13.34, 0) * mm});
            skLineSegment(sketch, "E38", {"start": v(13.34, 0) * mm, "end": v(12.7, 0) * mm});
            skSolve(sketch);
        }
        {
            var Q0;
            Q0 = qSketchRegion(id + "F15", true);
            var Q1;
            Q1=makeQuery(id+"F6.opExtrude","SWEPT_FACE",FACE,{"disambiguationData":[OSD([sQuery(id+"F5.wireOp",EDGE,"E14.0")])]});
            revolve(context, id + "F16", {"operationType" : NewBodyOperationType.REMOVE, "entities" : qUnion([Q0]), "axis" : qUnion([Q1]), "revolveType" : RevolveType.FULL, "oppositeDirection" : true});
        }
    });
